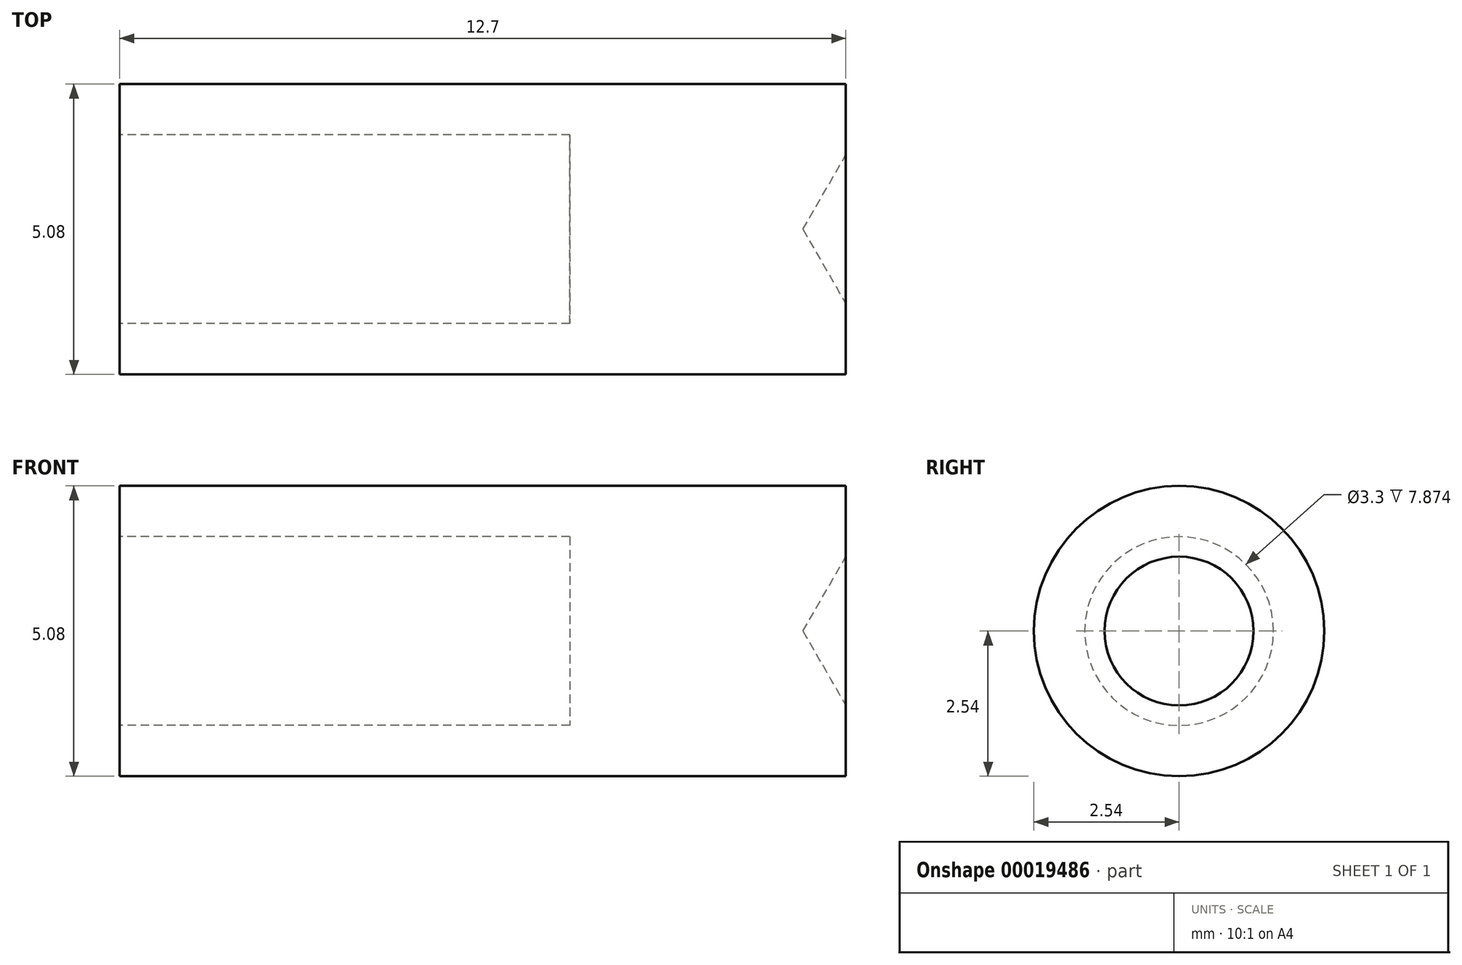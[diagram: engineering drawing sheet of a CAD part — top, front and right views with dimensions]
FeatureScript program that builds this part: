
annotation { "Feature Type Name" : "Feature", "Feature Type Description" : "" }
export const myFeature = defineFeature(function(context is Context, id is Id, definition is map)
    precondition{}
    {
        {
            var Q0;
            Q0=qCreatedBy(makeId("Front.planeOp"),FACE);
            var sketch = newSketch(context, id + "F0", { "sketchPlane" : qUnion([Q0])});
            skLineSegment(sketch, "E0", {"start": v(0, 0) * mm, "end": v(12.7, 0) * mm});
            skLineSegment(sketch, "E1", {"start": v(12.7, 0) * mm, "end": v(12.7, -1.24) * mm});
            skLineSegment(sketch, "E2", {"start": v(12.7, -1.24) * mm, "end": v(11.95, -2.54) * mm});
            skLineSegment(sketch, "E3", {"start": v(11.95, -2.54) * mm, "end": v(0, -2.54) * mm});
            skLineSegment(sketch, "E4", {"start": v(0, -2.54) * mm, "end": v(0, 0) * mm});
            skSolve(sketch);
        }
        {
            var Q0;
            Q0 = qSketchRegion(id + "F0", true);
            var Q1;
            Q1=sQuery(id+"F0.wireOp",EDGE,"E3");
            revolve(context, id + "F1", {"entities" : qUnion([Q0]), "axis" : qUnion([Q1]), "revolveType" : RevolveType.FULL});
        }
        {
            var Q0;
            Q0=makeQuery(id+"F1.opRevolve","SWEPT_FACE",FACE,{"disambiguationData":[OSD([sQuery(id+"F0.wireOp",EDGE,"E4")])]});
            var sketch = newSketch(context, id + "F2", { "sketchPlane" : qUnion([Q0])});
            skCircle(sketch, "E5", {"center": v(0, -2.54) * mm, "radius": 1.65 * mm});
            skSolve(sketch);
        }
        {
            var Q0;
            Q0 = qSketchRegion(id + "F2", true);
            extrude(context, id + "F3", {"entities" : qUnion([Q0]), "operationType" : NewBodyOperationType.REMOVE, "oppositeDirection" : true, "depth" : 7.87 * mm});
        }
    });
